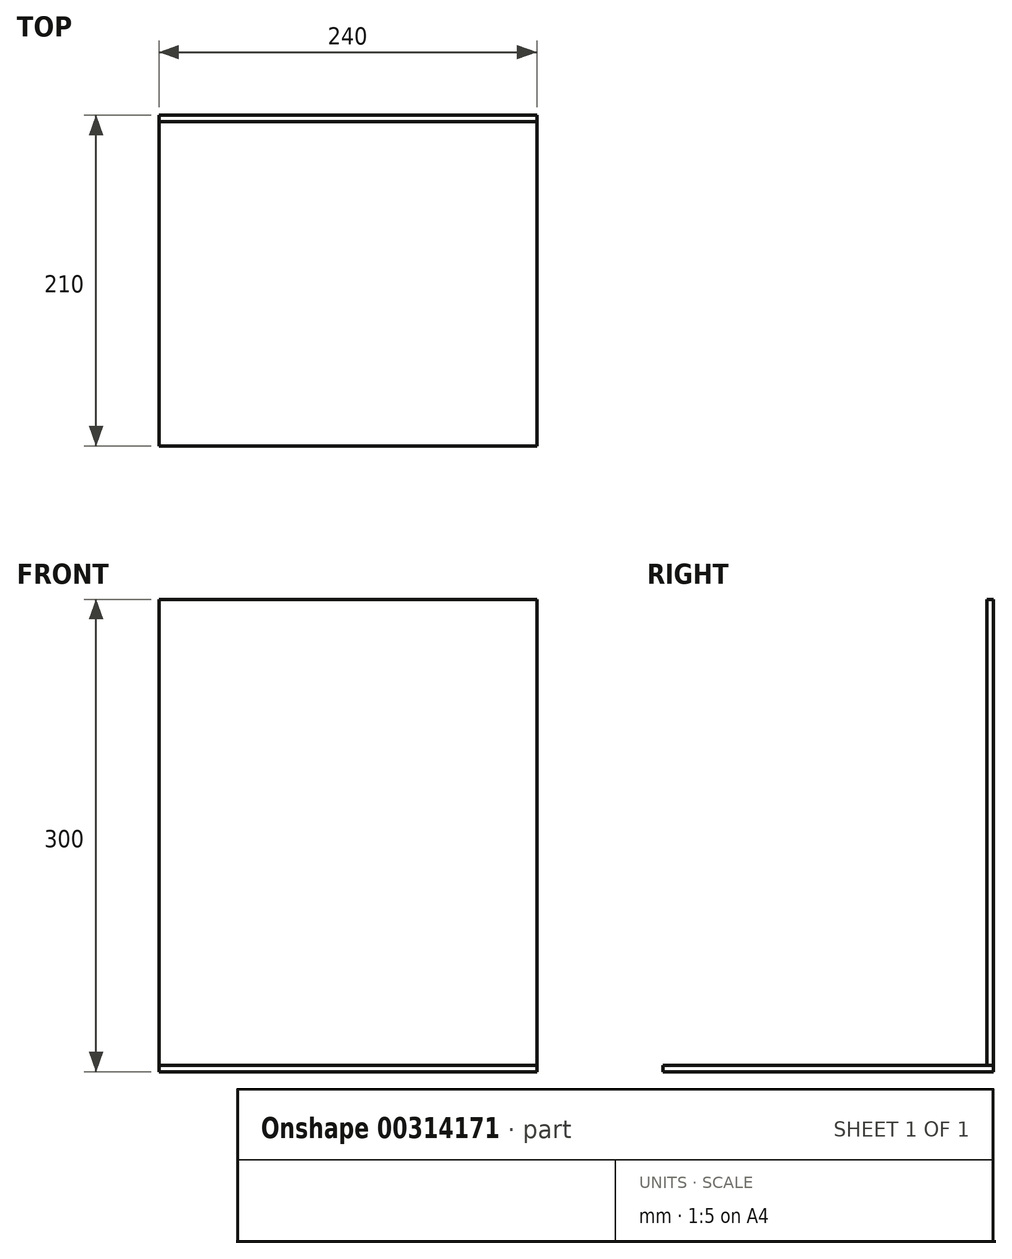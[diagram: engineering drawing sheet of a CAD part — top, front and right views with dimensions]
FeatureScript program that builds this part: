
annotation { "Feature Type Name" : "Feature", "Feature Type Description" : "" }
export const myFeature = defineFeature(function(context is Context, id is Id, definition is map)
    precondition{}
    {
        {
            var Q0;
            Q0=qCreatedBy(makeId("Top.planeOp"),FACE);
            var sketch = newSketch(context, id + "F0", { "sketchPlane" : qUnion([Q0])});
            skLineSegment(sketch, "E0.bottom", {"start": v(0, 0) * mm, "end": v(240, 0) * mm});
            skLineSegment(sketch, "E0.top", {"start": v(0, 210) * mm, "end": v(240, 210) * mm});
            skLineSegment(sketch, "E0.left", {"start": v(0, 0) * mm, "end": v(0, 210) * mm});
            skLineSegment(sketch, "E0.right", {"start": v(240, 0) * mm, "end": v(240, 210) * mm});
            skLineSegment(sketch, "E1.0", {"start": v(4, 4) * mm, "end": v(4, 206) * mm});
            skLineSegment(sketch, "E2.0", {"start": v(0, 206) * mm, "end": v(240, 206) * mm});
            skLineSegment(sketch, "E3.0", {"start": v(236, 4) * mm, "end": v(236, 206) * mm});
            skLineSegment(sketch, "E4.0", {"start": v(0, 4) * mm, "end": v(240, 4) * mm});
            skLineSegment(sketch, "E5.0", {"start": v(19, 4) * mm, "end": v(19, 206) * mm});
            skLineSegment(sketch, "E6.0", {"start": v(221, 4) * mm, "end": v(221, 206) * mm});
            skLineSegment(sketch, "E7.0", {"start": v(4, 191) * mm, "end": v(236, 191) * mm});
            skLineSegment(sketch, "E8.0", {"start": v(4, 19) * mm, "end": v(236, 19) * mm});
            skLineSegment(sketch, "E9.0", {"start": v(26, 4) * mm, "end": v(26, 19) * mm});
            skLineSegment(sketch, "E10.0", {"start": v(214, 4) * mm, "end": v(214, 19) * mm});
            skLineSegment(sketch, "E11.trimOffspring", {"start": v(26, 191) * mm, "end": v(26, 206) * mm});
            skLineSegment(sketch, "E12.trimOffspring", {"start": v(214, 191) * mm, "end": v(214, 206) * mm});
            skSolve(sketch);
        }
        {
            var Q0;
            {var subQ0=sQuery(id+"F0.wireOp",EDGE,"E2.0");var subQ6=sQuery(id+"F0.wireOp",EDGE,"E0.left");var subQ9=makeQuery(id+"F0.imprint","INTERSECT",VERTEX,{"derivedFrom":[subQ6,subQ0]});Q0=makeQuery(id+"F0.imprint","IMPRINT",FACE,{"disambiguationData":[TD([[makeQuery(id+"F0.imprint","IMPRINT",EDGE,{"disambiguationData":[TD([[subQ9,1.0]])],"derivedFrom":subQ6}),-1.0]])]});}
            var Q1;
            {var subQ1=sQuery(id+"F0.wireOp",EDGE,"E0.top");Q1=makeQuery(id+"F0.imprint","IMPRINT",FACE,{"disambiguationData":[TD([[makeQuery(id+"F0.imprint","IMPRINT",EDGE,{"derivedFrom":subQ1}),-1.0]])]});}
            var Q2;
            {var subQ4=sQuery(id+"F0.wireOp",EDGE,"E0.bottom");Q2=makeQuery(id+"F0.imprint","IMPRINT",FACE,{"disambiguationData":[TD([[makeQuery(id+"F0.imprint","IMPRINT",EDGE,{"derivedFrom":subQ4}),1.0]])]});}
            var Q3;
            {var subQ0=sQuery(id+"F0.wireOp",EDGE,"E7.0");var subQ1=sQuery(id+"F0.wireOp",EDGE,"E1.0");var subQ2=makeQuery(id+"F0.imprint","INTERSECT",VERTEX,{"derivedFrom":[subQ1,subQ0]});Q3=makeQuery(id+"F0.imprint","IMPRINT",FACE,{"disambiguationData":[TD([[makeQuery(id+"F0.imprint","IMPRINT",EDGE,{"disambiguationData":[TD([[subQ2,1.0]])],"derivedFrom":subQ1}),-1.0]])]});}
            var Q4;
            {var subQ0=sQuery(id+"F0.wireOp",EDGE,"E7.0");var subQ1=sQuery(id+"F0.wireOp",EDGE,"E3.0");var subQ2=makeQuery(id+"F0.imprint","INTERSECT",VERTEX,{"derivedFrom":[subQ1,subQ0]});Q4=makeQuery(id+"F0.imprint","IMPRINT",FACE,{"disambiguationData":[TD([[makeQuery(id+"F0.imprint","IMPRINT",EDGE,{"disambiguationData":[TD([[subQ2,1.0]])],"derivedFrom":subQ1}),1.0]])]});}
            var Q5;
            {var subQ3=sQuery(id+"F0.wireOp",EDGE,"E10.0");Q5=makeQuery(id+"F0.imprint","IMPRINT",FACE,{"disambiguationData":[TD([[makeQuery(id+"F0.imprint","IMPRINT",EDGE,{"derivedFrom":subQ3}),-1.0]])]});}
            var Q6;
            {var subQ0=sQuery(id+"F0.wireOp",EDGE,"E9.0");Q6=makeQuery(id+"F0.imprint","IMPRINT",FACE,{"disambiguationData":[TD([[makeQuery(id+"F0.imprint","IMPRINT",EDGE,{"derivedFrom":subQ0}),-1.0]])]});}
            var Q7;
            {var subQ3=sQuery(id+"F0.wireOp",EDGE,"E5.0");var subQ5=sQuery(id+"F0.wireOp",EDGE,"E8.0");var subQ9=makeQuery(id+"F0.imprint","INTERSECT",VERTEX,{"derivedFrom":[subQ3,subQ5]});Q7=makeQuery(id+"F0.imprint","IMPRINT",FACE,{"disambiguationData":[TD([[makeQuery(id+"F0.imprint","IMPRINT",EDGE,{"disambiguationData":[TD([[subQ9,-1.0]])],"derivedFrom":subQ3}),-1.0]])]});}
            var Q8;
            {var subQ5=sQuery(id+"F0.wireOp",EDGE,"E2.0");var subQ6=sQuery(id+"F0.wireOp",EDGE,"E0.right");var subQ7=makeQuery(id+"F0.imprint","INTERSECT",VERTEX,{"derivedFrom":[subQ6,subQ5]});Q8=makeQuery(id+"F0.imprint","IMPRINT",FACE,{"disambiguationData":[TD([[makeQuery(id+"F0.imprint","IMPRINT",EDGE,{"disambiguationData":[TD([[subQ7,1.0]])],"derivedFrom":subQ6}),1.0]])]});}
            var Q9;
            {var subQ0=sQuery(id+"F0.wireOp",EDGE,"E4.0");var subQ1=sQuery(id+"F0.wireOp",EDGE,"E1.0");var subQ2=makeQuery(id+"F0.imprint","INTERSECT",VERTEX,{"derivedFrom":[subQ1,subQ0]});Q9=makeQuery(id+"F0.imprint","IMPRINT",FACE,{"disambiguationData":[TD([[makeQuery(id+"F0.imprint","IMPRINT",EDGE,{"disambiguationData":[TD([[subQ2,-1.0]])],"derivedFrom":subQ1}),-1.0]])]});}
            var Q10;
            {var subQ3=sQuery(id+"F0.wireOp",EDGE,"E9.0");Q10=makeQuery(id+"F0.imprint","IMPRINT",FACE,{"disambiguationData":[TD([[makeQuery(id+"F0.imprint","IMPRINT",EDGE,{"derivedFrom":subQ3}),1.0]])]});}
            var Q11;
            {var subQ3=sQuery(id+"F0.wireOp",EDGE,"E11.trimOffspring");Q11=makeQuery(id+"F0.imprint","IMPRINT",FACE,{"disambiguationData":[TD([[makeQuery(id+"F0.imprint","IMPRINT",EDGE,{"derivedFrom":subQ3}),1.0]])]});}
            var Q12;
            {var subQ0=sQuery(id+"F0.wireOp",EDGE,"E2.0");var subQ1=sQuery(id+"F0.wireOp",EDGE,"E1.0");var subQ2=makeQuery(id+"F0.imprint","INTERSECT",VERTEX,{"derivedFrom":[subQ1,subQ0]});Q12=makeQuery(id+"F0.imprint","IMPRINT",FACE,{"disambiguationData":[TD([[makeQuery(id+"F0.imprint","IMPRINT",EDGE,{"disambiguationData":[TD([[subQ2,1.0]])],"derivedFrom":subQ1}),-1.0]])]});}
            var Q13;
            {var subQ0=sQuery(id+"F0.wireOp",EDGE,"E11.trimOffspring");Q13=makeQuery(id+"F0.imprint","IMPRINT",FACE,{"disambiguationData":[TD([[makeQuery(id+"F0.imprint","IMPRINT",EDGE,{"derivedFrom":subQ0}),-1.0]])]});}
            var Q14;
            {var subQ0=sQuery(id+"F0.wireOp",EDGE,"E3.0");var subQ1=sQuery(id+"F0.wireOp",EDGE,"E2.0");var subQ2=makeQuery(id+"F0.imprint","INTERSECT",VERTEX,{"derivedFrom":[subQ1,subQ0]});Q14=makeQuery(id+"F0.imprint","IMPRINT",FACE,{"disambiguationData":[TD([[makeQuery(id+"F0.imprint","IMPRINT",EDGE,{"disambiguationData":[TD([[subQ2,1.0]])],"derivedFrom":subQ1}),-1.0]])]});}
            var Q15;
            {var subQ3=sQuery(id+"F0.wireOp",EDGE,"E12.trimOffspring");Q15=makeQuery(id+"F0.imprint","IMPRINT",FACE,{"disambiguationData":[TD([[makeQuery(id+"F0.imprint","IMPRINT",EDGE,{"derivedFrom":subQ3}),-1.0]])]});}
            var Q16;
            {var subQ0=sQuery(id+"F0.wireOp",EDGE,"E4.0");var subQ1=sQuery(id+"F0.wireOp",EDGE,"E3.0");var subQ2=makeQuery(id+"F0.imprint","INTERSECT",VERTEX,{"derivedFrom":[subQ1,subQ0]});Q16=makeQuery(id+"F0.imprint","IMPRINT",FACE,{"disambiguationData":[TD([[makeQuery(id+"F0.imprint","IMPRINT",EDGE,{"disambiguationData":[TD([[subQ2,-1.0]])],"derivedFrom":subQ1}),1.0]])]});}
            extrude(context, id + "F1", {"entities" : qUnion([Q0, Q1, Q2, Q3, Q4, Q5, Q6, Q7, Q8, Q9, Q10, Q11, Q12, Q13, Q14, Q15, Q16]), "depth" : 4 * mm});
        }
        {
            var Q0;
            {var subQ1=sQuery(id+"F0.wireOp",EDGE,"E0.top");Q0=makeQuery(id+"F0.imprint","IMPRINT",FACE,{"disambiguationData":[TD([[makeQuery(id+"F0.imprint","IMPRINT",EDGE,{"derivedFrom":subQ1}),-1.0]])]});}
            extrude(context, id + "F2", {"entities" : qUnion([Q0]), "depth" : 300 * mm, "hasSecondDirection" : true, "secondDirectionOppositeDirection" : true, "secondDirectionDepth" : -4 * mm});
        }
    });
